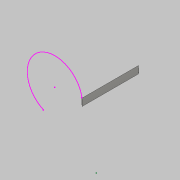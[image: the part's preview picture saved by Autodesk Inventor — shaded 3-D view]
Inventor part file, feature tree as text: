
AUTODESK INVENTOR PART (.ipt)
format: ipt  version: 2016 (Build 200138000, 138)  size: 70,144 bytes
history: native  units: in
note: dims shown in document units (in); Inventor stores cm internally (conversion verified against a paired STEP export)
features: sketch x2, extrude x1
ambient origin geometry x8: Origin, YZ Plane, XZ Plane, XY Plane, X Axis, Y Axis, Z Axis, Center Point
bodies: Solid1 (feature_tree)
feature tree (3):
  extrude  "Extrusion1"  [1 undecoded]
  sketch  "Sketch3"
  sketch  "Sketch1"  dims[d0=0.6in d1=0.0in]
note: 1 required parameter value undecoded (feature->parameter linkage not recoverable at this tier; creation-order binding heuristic only, values carry confidence <= 0.55)
